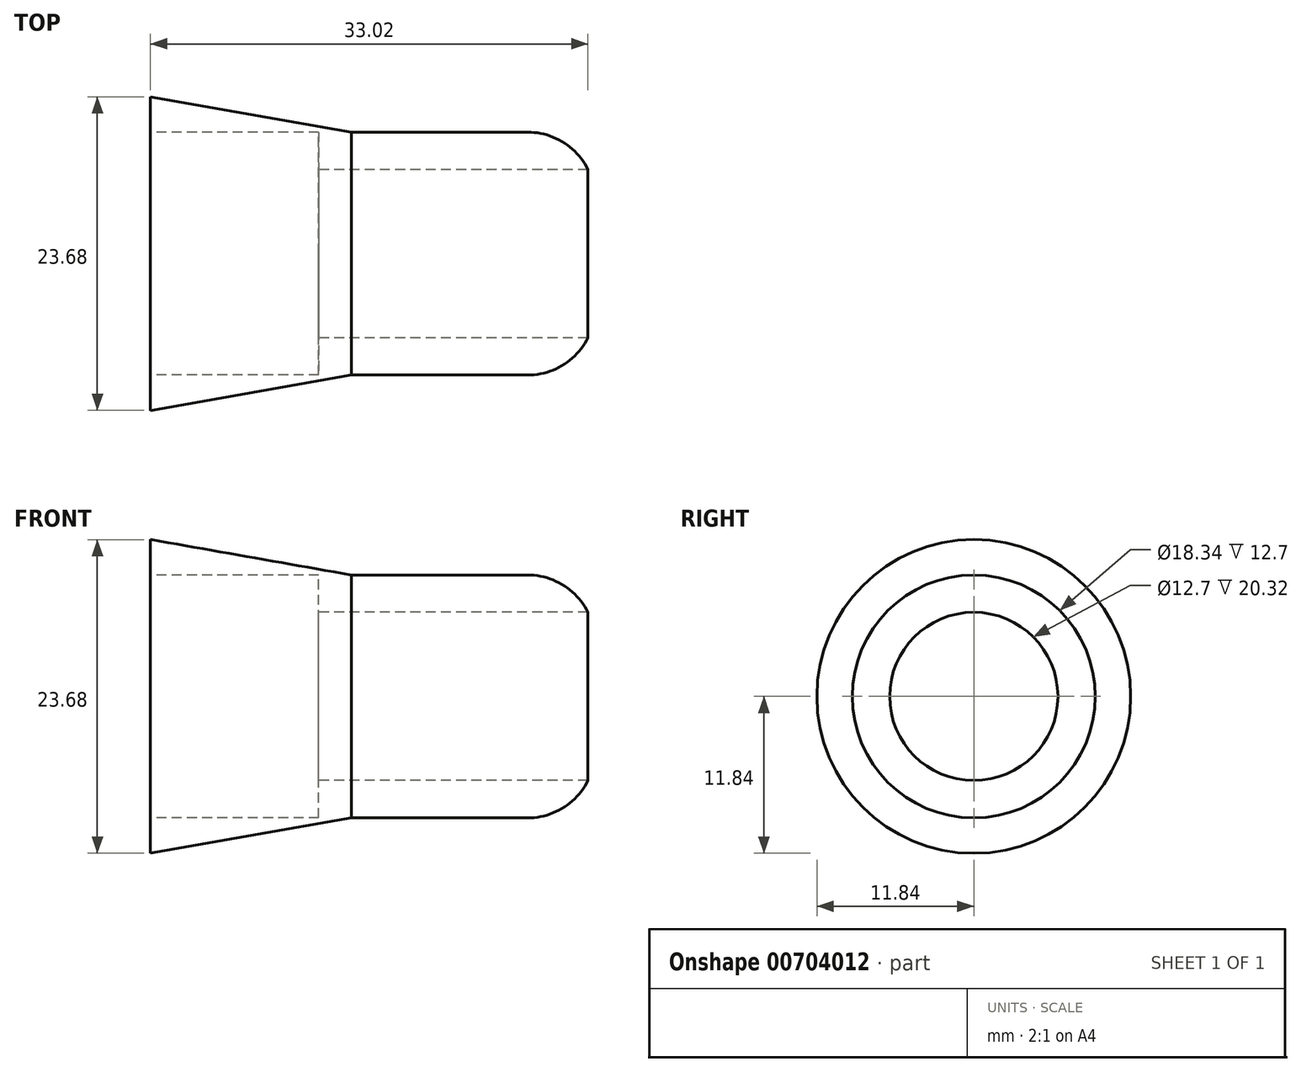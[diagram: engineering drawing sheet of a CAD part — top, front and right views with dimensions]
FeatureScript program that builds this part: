
annotation { "Feature Type Name" : "Feature", "Feature Type Description" : "" }
export const myFeature = defineFeature(function(context is Context, id is Id, definition is map)
    precondition{}
    {
        {
            var Q0;
            Q0=qCreatedBy(makeId("Right.planeOp"),FACE);
            var sketch = newSketch(context, id + "F0", { "sketchPlane" : qUnion([Q0])});
            skCircle(sketch, "E0", {"center": v(0, 0) * mm, "radius": 12.44 * mm});
            skCircle(sketch, "E1", {"center": v(0, 0) * mm, "radius": 9.17 * mm});
            skCircle(sketch, "E2", {"center": v(0, 0) * mm, "radius": 6.35 * mm});
            skSolve(sketch);
        }
        {
            var Q0;
            Q0=makeQuery(id+"F0.imprint","IMPRINT",FACE,{"disambiguationData":[TD([[makeQuery(id+"F0.imprint","IMPRINT",EDGE,{"derivedFrom":sQuery(id+"F0.wireOp",EDGE,"E0")}),1.0]])]});
            extrude(context, id + "F1", {"entities" : qUnion([Q0]), "endBound" : BoundingType.SYMMETRIC, "depth" : 25.4 * mm, "offsetDistance" : 25.4 * mm});
        }
        {
            var Q0;
            Q0=makeQuery(id+"F0.imprint","IMPRINT",FACE,{"disambiguationData":[TD([[makeQuery(id+"F0.imprint","IMPRINT",EDGE,{"derivedFrom":sQuery(id+"F0.wireOp",EDGE,"E1")}),1.0]])]});
            extrude(context, id + "F2", {"entities" : qUnion([Q0]), "operationType" : NewBodyOperationType.ADD, "depth" : 20.32 * mm, "offsetDistance" : 25.4 * mm});
        }
        {
            var Q0;
            Q0=makeQuery(id+"F1.opExtrude","CAP_EDGE",EDGE,{"disambiguationData":[OSD([sQuery(id+"F0.wireOp",EDGE,"E0")])],"isStart":false});
            chamfer(context, id + "F3", {"entities" : qUnion([Q0]), "chamferType" : ChamferType.OFFSET_ANGLE, "width" : 5.08 * mm, "oppositeDirection" : false, "angle" : 80 * degree, "tangentPropagation" : true});
        }
        {
            var Q0;
            Q0=makeQuery(id+"F2.opExtrude","CAP_EDGE",EDGE,{"disambiguationData":[OSD([sQuery(id+"F0.wireOp",EDGE,"E1")])],"isStart":false});
            fillet(context, id + "F4", {"entities" : qUnion([Q0]), "tangentPropagation" : true, "radius" : 5.08 * mm, "defaultsChanged" : false, "vertexSettings" : [], "allowEdgeOverflow" : false});
        }
    });
